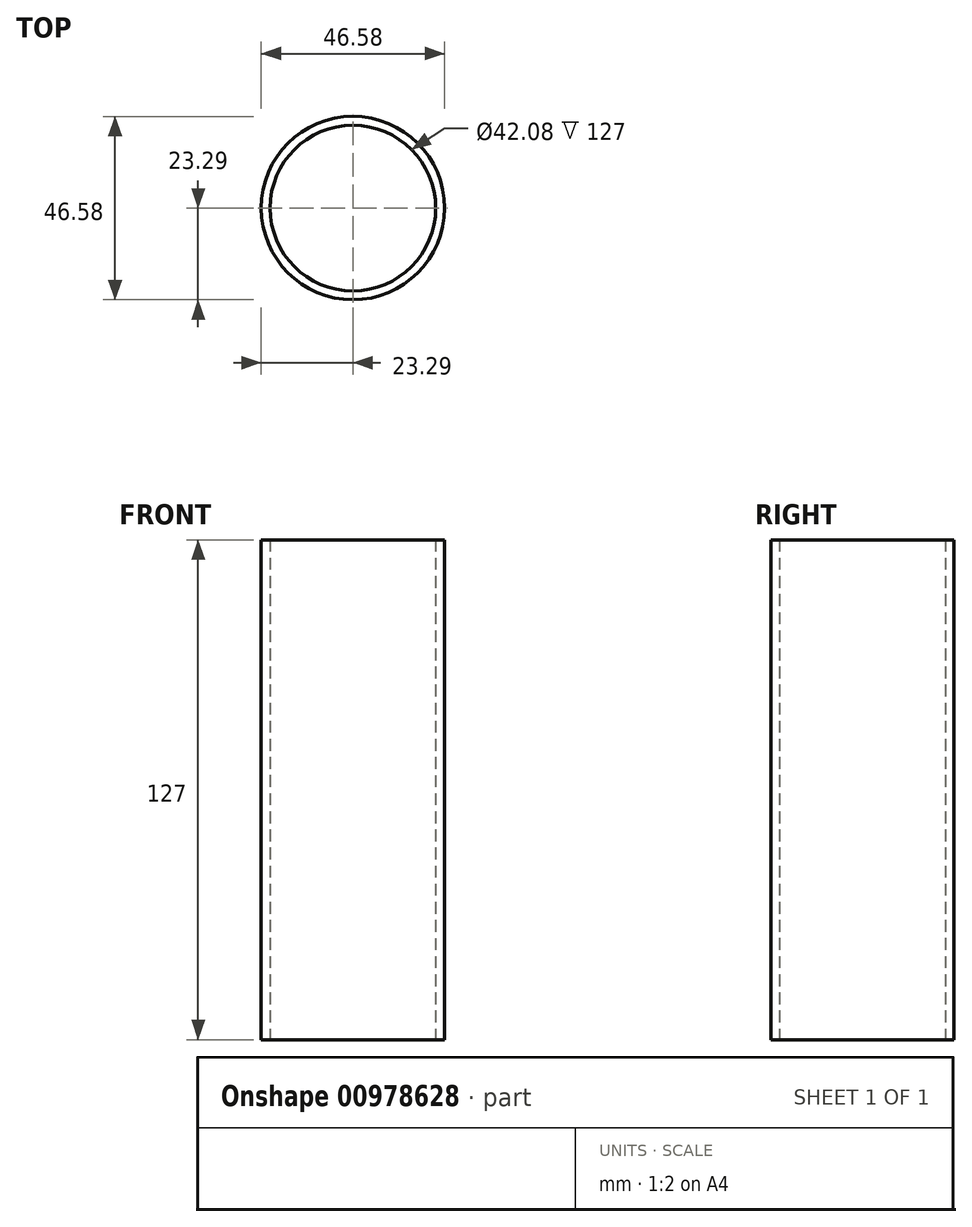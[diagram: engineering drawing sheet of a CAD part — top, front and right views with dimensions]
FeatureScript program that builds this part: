
annotation { "Feature Type Name" : "Feature", "Feature Type Description" : "" }
export const myFeature = defineFeature(function(context is Context, id is Id, definition is map)
    precondition{}
    {
        {
            var Q0;
            Q0=qCreatedBy(makeId("Top.planeOp"),FACE);
            var sketch = newSketch(context, id + "F0", { "sketchPlane" : qUnion([Q0])});
            skCircle(sketch, "E0", {"center": v(0, 0) * mm, "radius": 21.04 * mm});
            skSolve(sketch);
        }
        {
            var Q0;
            Q0=makeQuery(id+"F0.imprint","IMPRINT",FACE,{"disambiguationData":[TD([[makeQuery(id+"F0.imprint","IMPRINT",EDGE,{"derivedFrom":sQuery(id+"F0.wireOp",EDGE,"E0")}),1.0]])]});
            var sketch = newSketch(context, id + "F1", { "sketchPlane" : qUnion([Q0])});
            skCircle(sketch, "E1", {"center": v(0, 0) * mm, "radius": 23.3 * mm});
            skSolve(sketch);
        }
        {
            var Q0;
            Q0=makeQuery(id+"F1.imprint","IMPRINT",FACE,{"disambiguationData":[TD([[makeQuery(id+"F1.imprint","IMPRINT",EDGE,{"derivedFrom":sQuery(id+"F1.wireOp",EDGE,"E1")}),1.0]])]});
            var Q1;
            Q1=sQuery(id+"F0.wireOp",EDGE,"E0");
            var Q2;
            Q2=sQuery(id+"F1.wireOp",EDGE,"E1");
            extrude(context, id + "F2", {"entities" : qUnion([Q0]), "surfaceEntities" : qUnion([Q1, Q2]), "depth" : 25.4 * mm, "offsetDistance" : 25.4 * mm});
        }
        {
            var Q0;
            Q0=makeQuery(id+"F2.opExtrude","CAP_FACE",FACE,{"disambiguationData":[OSD([sQuery(id+"F0.wireOp",EDGE,"E0"),sQuery(id+"F1.wireOp",EDGE,"E1")])],"isStart":true});
            extrude(context, id + "F3", {"entities" : qUnion([Q0]), "operationType" : NewBodyOperationType.ADD, "depth" : 101.6 * mm, "offsetDistance" : 25.4 * mm});
        }
    });
